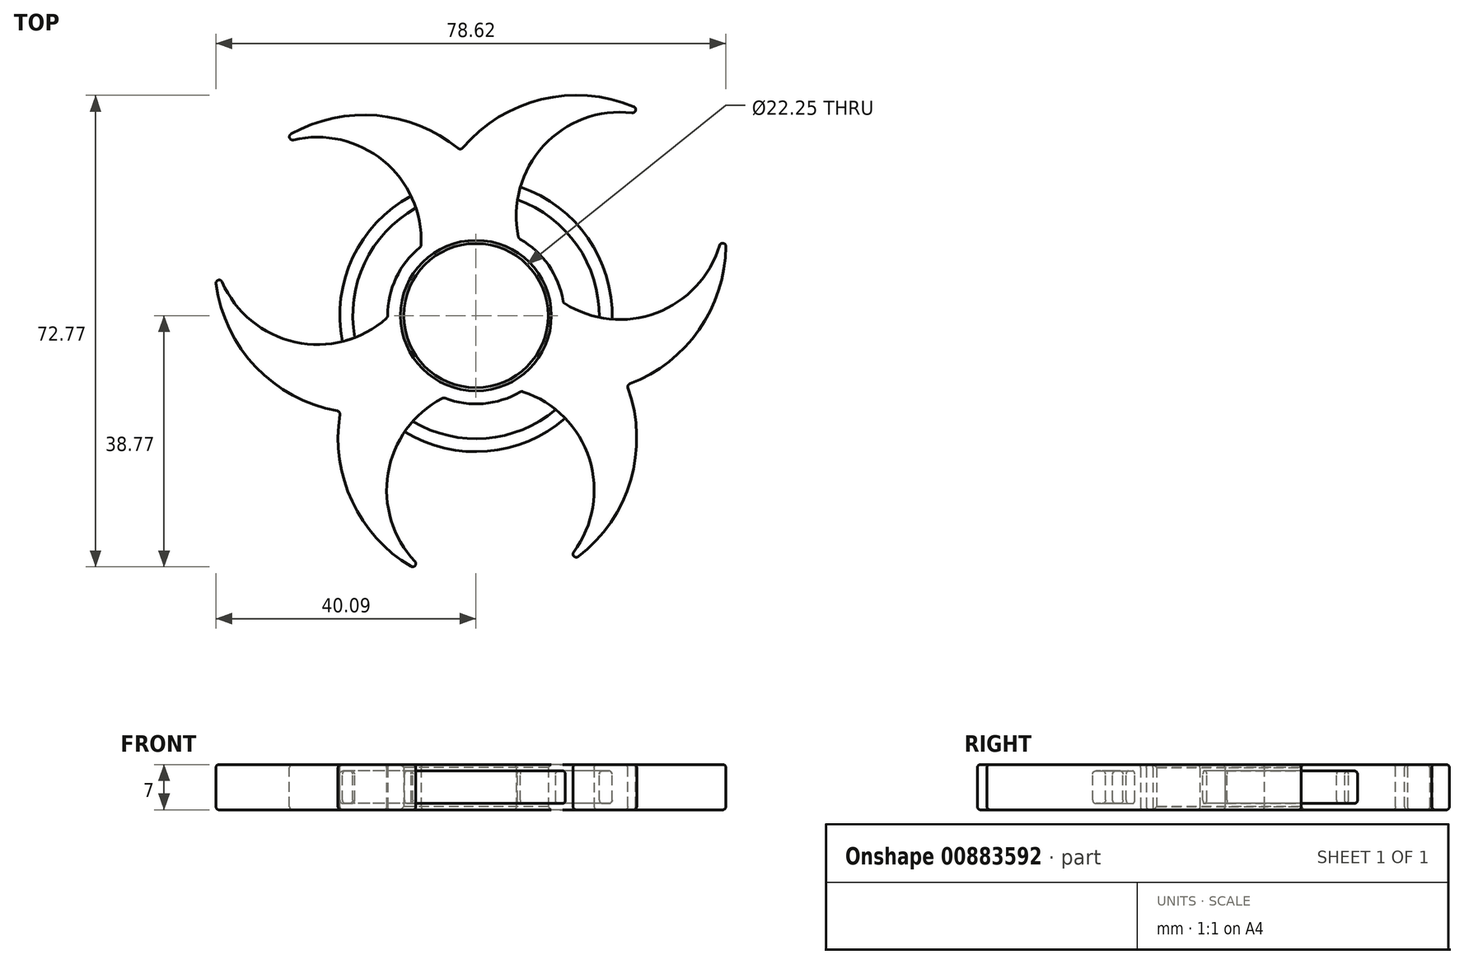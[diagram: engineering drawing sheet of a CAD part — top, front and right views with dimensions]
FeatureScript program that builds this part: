
annotation { "Feature Type Name" : "Feature", "Feature Type Description" : "" }
export const myFeature = defineFeature(function(context is Context, id is Id, definition is map)
    precondition{}
    {
        {
            var Q0;
            Q0=qCreatedBy(makeId("Top.planeOp"),FACE);
            var sketch = newSketch(context, id + "F0", { "sketchPlane" : qUnion([Q0])});
            skCircle(sketch, "E0", {"center": v(0, 0) * mm, "radius": 11.12 * mm});
            skArc(sketch, "E1", {"start": v(-5, -12.67) * mm, "mid": v(1.12, -13.58) * mm, "end": v(7.02, -11.68) * mm});
            skArc(sketch, "E2", {"start": v(-9.26, 16.59) * mm, "mid": v(-17.18, 8.11) * mm, "end": v(-18.7, -3.4) * mm});
            skArc(sketch, "E3", {"start": v(-10.02, 18.46) * mm, "mid": v(-19, 8.96) * mm, "end": v(-20.62, -4) * mm});
            skArc(sketch, "E4", {"start": v(28, 30.32) * mm, "mid": v(11.79, 27.53) * mm, "end": v(6.6, 11.92) * mm});
            skArc(sketch, "E5", {"start": v(28, 30.32) * mm, "mid": v(11.9, 33.72) * mm, "end": v(-2.37, 25.5) * mm});
            skArc(sketch, "E6.1.0", {"start": v(-40.26, 9.1) * mm, "mid": v(-35.15, -6.56) * mm, "end": v(-20.9, -14.8) * mm});
            skArc(sketch, "E6.1.1", {"start": v(-40.26, 9.1) * mm, "mid": v(-29.74, -3.56) * mm, "end": v(-13.62, -0.25) * mm});
            skArc(sketch, "E6.2.0", {"start": v(12.25, -39.4) * mm, "mid": v(23.25, -27.16) * mm, "end": v(23.26, -10.7) * mm});
            skArc(sketch, "E6.2.1", {"start": v(12.25, -39.4) * mm, "mid": v(17.95, -23.97) * mm, "end": v(7.02, -11.68) * mm});
            skArc(sketch, "E7.trimOffspring", {"start": v(-2.37, 25.5) * mm, "mid": v(-17.12, 30.96) * mm, "end": v(-31.94, 25.68) * mm});
            skArc(sketch, "E8.trimOffspring", {"start": v(-10.48, 3.73) * mm, "mid": v(-9.98, 4.7) * mm, "end": v(-9.54, 5.73) * mm});
            skArc(sketch, "E9.trimOffspring", {"start": v(-8.47, 10.67) * mm, "mid": v(-15.83, 25.02) * mm, "end": v(-31.94, 25.68) * mm});
            skArc(sketch, "E10.trimOffspring", {"start": v(8.47, 7.22) * mm, "mid": v(9.07, 6.28) * mm, "end": v(9.73, 5.4) * mm});
            skArc(sketch, "E11.trimOffspring", {"start": v(-20.9, -14.8) * mm, "mid": v(-18.25, -30.3) * mm, "end": v(-6.27, -40.5) * mm});
            skArc(sketch, "E12.trimOffspring", {"start": v(-10.98, -17.9) * mm, "mid": v(1.73, -20.93) * mm, "end": v(13.77, -15.86) * mm});
            skArc(sketch, "E13.trimOffspring", {"start": v(-9.74, -16.32) * mm, "mid": v(1.57, -18.94) * mm, "end": v(12.28, -14.5) * mm});
            skArc(sketch, "E14.trimOffspring", {"start": v(19, -0.27) * mm, "mid": v(15.62, 10.82) * mm, "end": v(6.41, 17.89) * mm});
            skArc(sketch, "E15.trimOffspring", {"start": v(21, -0.55) * mm, "mid": v(17.26, 11.96) * mm, "end": v(6.85, 19.85) * mm});
            skArc(sketch, "E16.trimOffspring", {"start": v(23.26, -10.7) * mm, "mid": v(35.37, -0.65) * mm, "end": v(38.2, 14.82) * mm});
            skArc(sketch, "E17.trimOffspring", {"start": v(2.01, -10.94) * mm, "mid": v(0.9, -11) * mm, "end": v(-0.19, -11.12) * mm});
            skArc(sketch, "E18.trimOffspring", {"start": v(-5, -12.67) * mm, "mid": v(-13.75, -26.22) * mm, "end": v(-6.27, -40.5) * mm});
            skArc(sketch, "E19.trimOffspring", {"start": v(13.6, 0.82) * mm, "mid": v(11.52, 7.27) * mm, "end": v(6.6, 11.92) * mm});
            skArc(sketch, "E20.trimOffspring", {"start": v(13.48, 2) * mm, "mid": v(29.58, 1.2) * mm, "end": v(38.2, 14.82) * mm});
            skArc(sketch, "E21.trimOffspring", {"start": v(-8.47, 10.67) * mm, "mid": v(-12.32, 5.82) * mm, "end": v(-13.62, -0.25) * mm});
            skSolve(sketch);
        }
        {
            var Q0;
            {var subQ2=sQuery(id+"F0.wireOp",EDGE,"E1");Q0=makeQuery(id+"F0.imprint","IMPRINT",FACE,{"disambiguationData":[TD([[makeQuery(id+"F0.imprint","IMPRINT",EDGE,{"derivedFrom":subQ2}),1.0]])]});}
            extrude(context, id + "F1", {"entities" : qUnion([Q0]), "depth" : 7 * mm, "offsetDistance" : 25 * mm});
        }
        {
            var Q0;
            {var subQ0=sQuery(id+"F0.wireOp",EDGE,"E12.trimOffspring");Q0=makeQuery(id+"F0.imprint","IMPRINT",FACE,{"disambiguationData":[TD([[makeQuery(id+"F0.imprint","IMPRINT",EDGE,{"derivedFrom":subQ0}),1.0]])]});}
            var Q1;
            {var subQ0=sQuery(id+"F0.wireOp",EDGE,"E2");Q1=makeQuery(id+"F0.imprint","IMPRINT",FACE,{"disambiguationData":[TD([[makeQuery(id+"F0.imprint","IMPRINT",EDGE,{"derivedFrom":subQ0}),-1.0]])]});}
            var Q2;
            {var subQ0=sQuery(id+"F0.wireOp",EDGE,"E14.trimOffspring");Q2=makeQuery(id+"F0.imprint","IMPRINT",FACE,{"disambiguationData":[TD([[makeQuery(id+"F0.imprint","IMPRINT",EDGE,{"derivedFrom":subQ0}),-1.0]])]});}
            extrude(context, id + "F2", {"entities" : qUnion([Q0, Q1, Q2]), "oppositeDirection" : true, "depth" : 5 * mm, "offsetDistance" : 25 * mm});
        }
        {
            var Q0;
            Q0=makeQuery(id+"F1.opExtrude","CAP_EDGE",EDGE,{"disambiguationData":[OSD([sQuery(id+"F0.wireOp",EDGE,"E20.trimOffspring")])],"isStart":false});
            var Q1;
            Q1=makeQuery(id+"F1.opExtrude","CAP_EDGE",EDGE,{"disambiguationData":[OSD([sQuery(id+"F0.wireOp",EDGE,"E6.1.1")])],"isStart":false});
            var Q2;
            Q2=makeQuery(id+"F1.opExtrude","CAP_EDGE",EDGE,{"disambiguationData":[OSD([sQuery(id+"F0.wireOp",EDGE,"E7.trimOffspring")])],"isStart":false});
            var Q3;
            Q3=makeQuery(id+"F1.opExtrude","CAP_EDGE",EDGE,{"disambiguationData":[OSD([sQuery(id+"F0.wireOp",EDGE,"E6.2.0")])],"isStart":true});
            var Q4;
            Q4=makeQuery(id+"F1.opExtrude","CAP_EDGE",EDGE,{"disambiguationData":[OSD([sQuery(id+"F0.wireOp",EDGE,"E6.2.1")])],"isStart":false});
            var Q5;
            Q5=makeQuery(id+"F1.opExtrude","CAP_EDGE",EDGE,{"disambiguationData":[OSD([sQuery(id+"F0.wireOp",EDGE,"E7.trimOffspring")])],"isStart":true});
            var Q6;
            Q6=makeQuery(id+"F1.opExtrude","CAP_EDGE",EDGE,{"disambiguationData":[OSD([sQuery(id+"F0.wireOp",EDGE,"E16.trimOffspring")])],"isStart":true});
            var Q7;
            Q7=makeQuery(id+"F1.opExtrude","CAP_EDGE",EDGE,{"disambiguationData":[OSD([sQuery(id+"F0.wireOp",EDGE,"E11.trimOffspring")])],"isStart":false});
            var Q8;
            Q8=makeQuery(id+"F1.opExtrude","SWEPT_EDGE",EDGE,{"disambiguationData":[OSD([sQuery(id+"F0.wireOp",EDGE,"E5"),sQuery(id+"F0.wireOp",EDGE,"E7.trimOffspring")])]});
            var Q9;
            Q9=makeQuery(id+"F1.opExtrude","CAP_EDGE",EDGE,{"disambiguationData":[OSD([sQuery(id+"F0.wireOp",EDGE,"E4")])],"isStart":false});
            var Q10;
            Q10=makeQuery(id+"F1.opExtrude","CAP_EDGE",EDGE,{"disambiguationData":[OSD([sQuery(id+"F0.wireOp",EDGE,"E21.trimOffspring")])],"isStart":true});
            var Q11;
            Q11=makeQuery(id+"F1.opExtrude","CAP_EDGE",EDGE,{"disambiguationData":[OSD([sQuery(id+"F0.wireOp",EDGE,"E9.trimOffspring")])],"isStart":false});
            var Q12;
            Q12=makeQuery(id+"F1.opExtrude","CAP_EDGE",EDGE,{"disambiguationData":[OSD([sQuery(id+"F0.wireOp",EDGE,"E1")])],"isStart":false});
            var Q13;
            Q13=makeQuery(id+"F1.opExtrude","CAP_EDGE",EDGE,{"disambiguationData":[OSD([sQuery(id+"F0.wireOp",EDGE,"E5")])],"isStart":false});
            var Q14;
            Q14=makeQuery(id+"F1.opExtrude","CAP_EDGE",EDGE,{"disambiguationData":[OSD([sQuery(id+"F0.wireOp",EDGE,"E4")])],"isStart":true});
            var Q15;
            Q15=makeQuery(id+"F1.opExtrude","CAP_EDGE",EDGE,{"disambiguationData":[OSD([sQuery(id+"F0.wireOp",EDGE,"E16.trimOffspring")])],"isStart":false});
            var Q16;
            Q16=makeQuery(id+"F1.opExtrude","CAP_EDGE",EDGE,{"disambiguationData":[OSD([sQuery(id+"F0.wireOp",EDGE,"E19.trimOffspring")])],"isStart":false});
            var Q17;
            Q17=makeQuery(id+"F1.opExtrude","CAP_EDGE",EDGE,{"disambiguationData":[OSD([sQuery(id+"F0.wireOp",EDGE,"E18.trimOffspring")])],"isStart":true});
            var Q18;
            Q18=makeQuery(id+"F1.opExtrude","CAP_EDGE",EDGE,{"disambiguationData":[OSD([sQuery(id+"F0.wireOp",EDGE,"E6.1.1")])],"isStart":true});
            var Q19;
            Q19=makeQuery(id+"F1.opExtrude","CAP_EDGE",EDGE,{"disambiguationData":[OSD([sQuery(id+"F0.wireOp",EDGE,"E6.2.0")])],"isStart":false});
            var Q20;
            Q20=makeQuery(id+"F1.opExtrude","CAP_EDGE",EDGE,{"disambiguationData":[OSD([sQuery(id+"F0.wireOp",EDGE,"E21.trimOffspring")])],"isStart":false});
            var Q21;
            Q21=makeQuery(id+"F1.opExtrude","CAP_EDGE",EDGE,{"disambiguationData":[OSD([sQuery(id+"F0.wireOp",EDGE,"E18.trimOffspring")])],"isStart":false});
            var Q22;
            Q22=makeQuery(id+"F1.opExtrude","CAP_EDGE",EDGE,{"disambiguationData":[OSD([sQuery(id+"F0.wireOp",EDGE,"E20.trimOffspring")])],"isStart":true});
            var Q23;
            Q23=makeQuery(id+"F1.opExtrude","CAP_EDGE",EDGE,{"disambiguationData":[OSD([sQuery(id+"F0.wireOp",EDGE,"E5")])],"isStart":true});
            var Q24;
            Q24=makeQuery(id+"F1.opExtrude","CAP_EDGE",EDGE,{"disambiguationData":[OSD([sQuery(id+"F0.wireOp",EDGE,"E19.trimOffspring")])],"isStart":true});
            var Q25;
            Q25=makeQuery(id+"F1.opExtrude","CAP_EDGE",EDGE,{"disambiguationData":[OSD([sQuery(id+"F0.wireOp",EDGE,"E6.1.0")])],"isStart":false});
            var Q26;
            Q26=makeQuery(id+"F1.opExtrude","SWEPT_EDGE",EDGE,{"disambiguationData":[OSD([sQuery(id+"F0.wireOp",EDGE,"E4"),sQuery(id+"F0.wireOp",EDGE,"E19.trimOffspring")])]});
            var Q27;
            Q27=makeQuery(id+"F1.opExtrude","SWEPT_EDGE",EDGE,{"disambiguationData":[OSD([sQuery(id+"F0.wireOp",EDGE,"E16.trimOffspring"),sQuery(id+"F0.wireOp",EDGE,"E20.trimOffspring")])]});
            var Q28;
            Q28=makeQuery(id+"F1.opExtrude","SWEPT_EDGE",EDGE,{"disambiguationData":[OSD([sQuery(id+"F0.wireOp",EDGE,"E6.1.0"),sQuery(id+"F0.wireOp",EDGE,"E11.trimOffspring")])]});
            var Q29;
            Q29=makeQuery(id+"F1.opExtrude","CAP_EDGE",EDGE,{"disambiguationData":[OSD([sQuery(id+"F0.wireOp",EDGE,"E6.1.0")])],"isStart":true});
            var Q30;
            Q30=makeQuery(id+"F1.opExtrude","SWEPT_EDGE",EDGE,{"disambiguationData":[OSD([sQuery(id+"F0.wireOp",EDGE,"E9.trimOffspring"),sQuery(id+"F0.wireOp",EDGE,"E21.trimOffspring")])]});
            var Q31;
            Q31=makeQuery(id+"F1.opExtrude","CAP_EDGE",EDGE,{"disambiguationData":[OSD([sQuery(id+"F0.wireOp",EDGE,"E1")])],"isStart":true});
            var Q32;
            Q32=makeQuery(id+"F1.opExtrude","CAP_EDGE",EDGE,{"disambiguationData":[OSD([sQuery(id+"F0.wireOp",EDGE,"E9.trimOffspring")])],"isStart":true});
            var Q33;
            Q33=makeQuery(id+"F1.opExtrude","SWEPT_EDGE",EDGE,{"disambiguationData":[OSD([sQuery(id+"F0.wireOp",EDGE,"E1"),sQuery(id+"F0.wireOp",EDGE,"E6.2.1")])]});
            var Q34;
            Q34=makeQuery(id+"F1.opExtrude","SWEPT_EDGE",EDGE,{"disambiguationData":[OSD([sQuery(id+"F0.wireOp",EDGE,"E19.trimOffspring"),sQuery(id+"F0.wireOp",EDGE,"E20.trimOffspring")])]});
            var Q35;
            Q35=makeQuery(id+"F1.opExtrude","SWEPT_EDGE",EDGE,{"disambiguationData":[OSD([sQuery(id+"F0.wireOp",EDGE,"E6.1.1"),sQuery(id+"F0.wireOp",EDGE,"E21.trimOffspring")])]});
            var Q36;
            Q36=makeQuery(id+"F1.opExtrude","SWEPT_EDGE",EDGE,{"disambiguationData":[OSD([sQuery(id+"F0.wireOp",EDGE,"E11.trimOffspring"),sQuery(id+"F0.wireOp",EDGE,"E18.trimOffspring")])]});
            var Q37;
            Q37=makeQuery(id+"F1.opExtrude","SWEPT_EDGE",EDGE,{"disambiguationData":[OSD([sQuery(id+"F0.wireOp",EDGE,"E6.2.0"),sQuery(id+"F0.wireOp",EDGE,"E6.2.1")])]});
            var Q38;
            Q38=makeQuery(id+"F1.opExtrude","SWEPT_EDGE",EDGE,{"disambiguationData":[OSD([sQuery(id+"F0.wireOp",EDGE,"E7.trimOffspring"),sQuery(id+"F0.wireOp",EDGE,"E9.trimOffspring")])]});
            var Q39;
            Q39=makeQuery(id+"F1.opExtrude","SWEPT_EDGE",EDGE,{"disambiguationData":[OSD([sQuery(id+"F0.wireOp",EDGE,"E4"),sQuery(id+"F0.wireOp",EDGE,"E5")])]});
            var Q40;
            Q40=makeQuery(id+"F1.opExtrude","CAP_EDGE",EDGE,{"disambiguationData":[OSD([sQuery(id+"F0.wireOp",EDGE,"E6.2.1")])],"isStart":true});
            var Q41;
            Q41=makeQuery(id+"F1.opExtrude","CAP_EDGE",EDGE,{"disambiguationData":[OSD([sQuery(id+"F0.wireOp",EDGE,"E11.trimOffspring")])],"isStart":true});
            var Q42;
            Q42=makeQuery(id+"F1.opExtrude","SWEPT_EDGE",EDGE,{"disambiguationData":[OSD([sQuery(id+"F0.wireOp",EDGE,"E1"),sQuery(id+"F0.wireOp",EDGE,"E18.trimOffspring")])]});
            var Q43;
            Q43=makeQuery(id+"F1.opExtrude","SWEPT_EDGE",EDGE,{"disambiguationData":[OSD([sQuery(id+"F0.wireOp",EDGE,"E6.2.0"),sQuery(id+"F0.wireOp",EDGE,"E16.trimOffspring")])]});
            var Q44;
            Q44=makeQuery(id+"F1.opExtrude","SWEPT_EDGE",EDGE,{"disambiguationData":[OSD([sQuery(id+"F0.wireOp",EDGE,"E6.1.0"),sQuery(id+"F0.wireOp",EDGE,"E6.1.1")])]});
            fillet(context, id + "F3", {"entities" : qUnion([Q0, Q1, Q2, Q3, Q4, Q5, Q6, Q7, Q8, Q9, Q10, Q11, Q12, Q13, Q14, Q15, Q16, Q17, Q18, Q19, Q20, Q21, Q22, Q23, Q24, Q25, Q26, Q27, Q28, Q29, Q30, Q31, Q32, Q33, Q34, Q35, Q36, Q37, Q38, Q39, Q40, Q41, Q42, Q43, Q44]), "radius" : 0.5 * mm, "tangentPropagation" : true, "allowEdgeOverflow" : false});
        }
        {
            var Q0;
            Q0=makeQuery(id+"F1.opExtrude","CAP_EDGE",EDGE,{"disambiguationData":[OSD([sQuery(id+"F0.wireOp",EDGE,"E0")])],"isStart":false});
            var Q1;
            Q1=makeQuery(id+"F1.opExtrude","CAP_EDGE",EDGE,{"disambiguationData":[OSD([sQuery(id+"F0.wireOp",EDGE,"E0")])],"isStart":true});
            chamfer(context, id + "F4", {"entities" : qUnion([Q0, Q1]), "width" : 0.5 * mm, "tangentPropagation" : true});
        }
        {
            var Q0;
            Q0=makeQuery(id+"F2.opExtrude","SWEPT_BODY",BODY,{"disambiguationData":[OSD([sQuery(id+"F0.wireOp",EDGE,"E2"),sQuery(id+"F0.wireOp",EDGE,"E3"),sQuery(id+"F0.wireOp",EDGE,"E6.1.1"),sQuery(id+"F0.wireOp",EDGE,"E9.trimOffspring")])]});
            var Q1;
            Q1=makeQuery(id+"F2.opExtrude","SWEPT_BODY",BODY,{"disambiguationData":[OSD([sQuery(id+"F0.wireOp",EDGE,"E4"),sQuery(id+"F0.wireOp",EDGE,"E14.trimOffspring"),sQuery(id+"F0.wireOp",EDGE,"E15.trimOffspring"),sQuery(id+"F0.wireOp",EDGE,"E20.trimOffspring")])]});
            var Q2;
            Q2=makeQuery(id+"F2.opExtrude","SWEPT_BODY",BODY,{"disambiguationData":[OSD([sQuery(id+"F0.wireOp",EDGE,"E6.2.1"),sQuery(id+"F0.wireOp",EDGE,"E12.trimOffspring"),sQuery(id+"F0.wireOp",EDGE,"E13.trimOffspring"),sQuery(id+"F0.wireOp",EDGE,"E18.trimOffspring")])]});
            transform(context, id + "F5", {"entities" : qUnion([Q0, Q1, Q2]), "transformType" : TransformType.TRANSLATION_3D, "dx" : 0 * mm, "dy" : 0 * mm, "dz" : 6 * mm, "makeCopy" : false});
        }
        {
            var Q0;
            Q0=makeQuery(id+"F2.opExtrude","CAP_EDGE",EDGE,{"disambiguationData":[OSD([sQuery(id+"F0.wireOp",EDGE,"E3")])],"isStart":true});
            var Q1;
            Q1=makeQuery(id+"F2.opExtrude","CAP_EDGE",EDGE,{"disambiguationData":[OSD([sQuery(id+"F0.wireOp",EDGE,"E2")])],"isStart":false});
            var Q2;
            Q2=makeQuery(id+"F2.opExtrude","CAP_EDGE",EDGE,{"disambiguationData":[OSD([sQuery(id+"F0.wireOp",EDGE,"E2")])],"isStart":true});
            var Q3;
            Q3=makeQuery(id+"F2.opExtrude","CAP_EDGE",EDGE,{"disambiguationData":[OSD([sQuery(id+"F0.wireOp",EDGE,"E3")])],"isStart":false});
            var Q4;
            Q4=makeQuery(id+"F2.opExtrude","CAP_EDGE",EDGE,{"disambiguationData":[OSD([sQuery(id+"F0.wireOp",EDGE,"E12.trimOffspring")])],"isStart":false});
            var Q5;
            Q5=makeQuery(id+"F2.opExtrude","CAP_EDGE",EDGE,{"disambiguationData":[OSD([sQuery(id+"F0.wireOp",EDGE,"E12.trimOffspring")])],"isStart":true});
            var Q6;
            Q6=makeQuery(id+"F2.opExtrude","CAP_EDGE",EDGE,{"disambiguationData":[OSD([sQuery(id+"F0.wireOp",EDGE,"E13.trimOffspring")])],"isStart":true});
            var Q7;
            Q7=makeQuery(id+"F2.opExtrude","CAP_EDGE",EDGE,{"disambiguationData":[OSD([sQuery(id+"F0.wireOp",EDGE,"E13.trimOffspring")])],"isStart":false});
            var Q8;
            Q8=makeQuery(id+"F2.opExtrude","CAP_EDGE",EDGE,{"disambiguationData":[OSD([sQuery(id+"F0.wireOp",EDGE,"E15.trimOffspring")])],"isStart":true});
            var Q9;
            Q9=makeQuery(id+"F2.opExtrude","CAP_EDGE",EDGE,{"disambiguationData":[OSD([sQuery(id+"F0.wireOp",EDGE,"E14.trimOffspring")])],"isStart":true});
            var Q10;
            Q10=makeQuery(id+"F2.opExtrude","CAP_EDGE",EDGE,{"disambiguationData":[OSD([sQuery(id+"F0.wireOp",EDGE,"E15.trimOffspring")])],"isStart":false});
            var Q11;
            Q11=makeQuery(id+"F2.opExtrude","CAP_EDGE",EDGE,{"disambiguationData":[OSD([sQuery(id+"F0.wireOp",EDGE,"E14.trimOffspring")])],"isStart":false});
            fillet(context, id + "F6", {"entities" : qUnion([Q0, Q1, Q2, Q3, Q4, Q5, Q6, Q7, Q8, Q9, Q10, Q11]), "radius" : 0.5 * mm, "tangentPropagation" : true, "allowEdgeOverflow" : false});
        }
        {
            var Q0;
            Q0=qCreatedBy(makeId("Top.planeOp"),FACE);
            var sketch = newSketch(context, id + "F7", { "sketchPlane" : qUnion([Q0])});
            skCircle(sketch, "E22", {"center": v(26.5, 19.52) * mm, "radius": 11.25 * mm});
            skCircle(sketch, "E23", {"center": v(26.5, 19.52) * mm, "radius": 5 * mm});
            skCircle(sketch, "E24", {"center": v(26.5, 19.52) * mm, "radius": 3.8 * mm});
            skCircle(sketch, "E25", {"center": v(26.5, 19.52) * mm, "radius": 1.5 * mm});
            skSolve(sketch);
        }
        {
            var Q0;
            Q0 = qSketchRegion(id + "F7", true);
            extrude(context, id + "F8", {"entities" : qUnion([Q0]), "depth" : 2 * mm, "offsetDistance" : 25 * mm});
        }
        {
            var Q0;
            Q0=makeQuery(id+"F7.imprint","IMPRINT",FACE,{"disambiguationData":[TD([[makeQuery(id+"F7.imprint","IMPRINT",EDGE,{"derivedFrom":sQuery(id+"F7.wireOp",EDGE,"E23")}),1.0]])]});
            extrude(context, id + "F9", {"entities" : qUnion([Q0]), "operationType" : NewBodyOperationType.ADD, "depth" : 3 * mm, "offsetDistance" : 25 * mm});
        }
        {
            var Q0;
            Q0=makeQuery(id+"F7.imprint","IMPRINT",FACE,{"disambiguationData":[TD([[makeQuery(id+"F7.imprint","IMPRINT",EDGE,{"derivedFrom":sQuery(id+"F7.wireOp",EDGE,"E24")}),1.0]])]});
            extrude(context, id + "F10", {"entities" : qUnion([Q0]), "operationType" : NewBodyOperationType.ADD, "depth" : 6.25 * mm, "offsetDistance" : 25 * mm});
        }
        {
            var Q0;
            Q0=makeQuery(id+"F10.opExtrude","CAP_EDGE",EDGE,{"disambiguationData":[OSD([sQuery(id+"F7.wireOp",EDGE,"E25")])],"isStart":false});
            var Q1;
            Q1=makeQuery(id+"F8.opExtrude","CAP_EDGE",EDGE,{"disambiguationData":[OSD([sQuery(id+"F7.wireOp",EDGE,"E22")])],"isStart":false});
            var Q2;
            Q2=makeQuery(id+"F9.opExtrude","CAP_EDGE",EDGE,{"disambiguationData":[OSD([sQuery(id+"F7.wireOp",EDGE,"E23")])],"isStart":false});
            var Q3;
            Q3=makeQuery(id+"F8.opExtrude","CAP_EDGE",EDGE,{"disambiguationData":[OSD([sQuery(id+"F7.wireOp",EDGE,"E23")])],"isStart":false});
            var Q4;
            Q4=makeQuery(id+"F8.opExtrude","CAP_EDGE",EDGE,{"disambiguationData":[OSD([sQuery(id+"F7.wireOp",EDGE,"E22")])],"isStart":true});
            var Q5;
            Q5=makeQuery(id+"F10.opExtrude","CAP_EDGE",EDGE,{"disambiguationData":[OSD([sQuery(id+"F7.wireOp",EDGE,"E25")])],"isStart":true});
            fillet(context, id + "F11", {"entities" : qUnion([Q0, Q1, Q2, Q3, Q4, Q5]), "radius" : 0.5 * mm, "tangentPropagation" : true, "allowEdgeOverflow" : false});
        }
        {
            var Q0;
            Q0=makeQuery(id+"F10.opExtrude","CAP_EDGE",EDGE,{"disambiguationData":[OSD([sQuery(id+"F7.wireOp",EDGE,"E24")])],"isStart":false});
            chamfer(context, id + "F12", {"entities" : qUnion([Q0]), "width" : 0.5 * mm, "tangentPropagation" : true});
        }
        {
            var Q0;
            Q0=makeQuery(id+"F8.opExtrude","SWEPT_BODY",BODY,{"disambiguationData":[OSD([sQuery(id+"F7.wireOp",EDGE,"E22"),sQuery(id+"F7.wireOp",EDGE,"E23")])]});
            deleteBodies(context, id + "F13", {"entities" : qUnion([Q0])});
        }
    });
